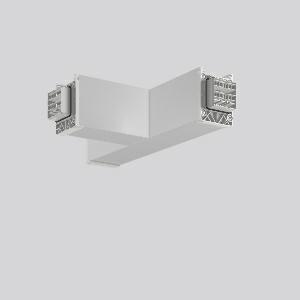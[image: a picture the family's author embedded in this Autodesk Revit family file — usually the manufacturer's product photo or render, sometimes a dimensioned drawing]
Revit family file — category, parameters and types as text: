
# Revit family: linedo_t-verbindung_982774_000_2_908e
name_source: partatom
category: Lighting Fixtures
units: mm (PartAtom-declared; Revit-internal decimal feet)

## family parameters
Cut with Voids When Loaded = No
Host = Face
Light Source = No
Part Type = Normal
Room Calculation Point = No
Round Connector Dimension = Use Diameter
Shared = No

## types (1)
- LINEDO T-Verbindung
    Apparent Load = 0 VA
    Default Elevation = 1800 mm
    Description = Series: LINEDO
T-connector, 14-pole, connection plug / socket - plug. Housing: extruded aluminium profile, anodised. Cover made of plastic, surface like housing. LINEDO plug system, plastic, light grey. Easy connection for rigid or flexible wires. 5 membrane cable entries (2 x M20 and 3 x M25). Suitable for power supply in 7-pole version. Ready prewired. Colour-coded individual cables enable easy electromechanical separation.
Colour: anodised aluminium
Length: 330 mm
Width: 204 mm
Height: 76 mm
Weight: 1070 g
    Height = 76 mm
    Lamp = 0 x
    Length = 331 mm
    Luminous efficacy = 0 lm/W
    Manufacturer = RZB
    ModVariant = No
    Model = 982774.000.2
    Mounting Place = Ceiling
    Mounting Type = Surface mounted
    Number of Poles = 1
    OnlyDefault = Yes
    Power Factor = 1
    Product Name = LINEDO T-Verbindung
    Product group = Continuous line luminaire system Linedo IP 54
    ProductGroupID = 314
    Protection Class = Protection class I
    Protection Degree = Degree of protection
    RLX_Detail_Level = 1
    RLX_Emergency_Light_Flux = 0 lm
    RLX_Emergency_Type = 0
    RLX_Emergency_Type_DB = No
    RlxData = <blob elided: 18249 chars, md5=d18dbb0c>
    Standby Power = 0 W
    System Light Flux = 0 lm
    System Power = 0 W
    Type Comments = Product without accessories
    Type Image = 982774.000.2.jpg
    URL = http://relux.com
    VarID = ---
    Voltage = 0 V
    Weight = 0.00 kg
    Width = 204 mm

## geometry (parser evidence)
native form markers: Blend x4, Sweep x11
no freeform markers — native parametric forms only
